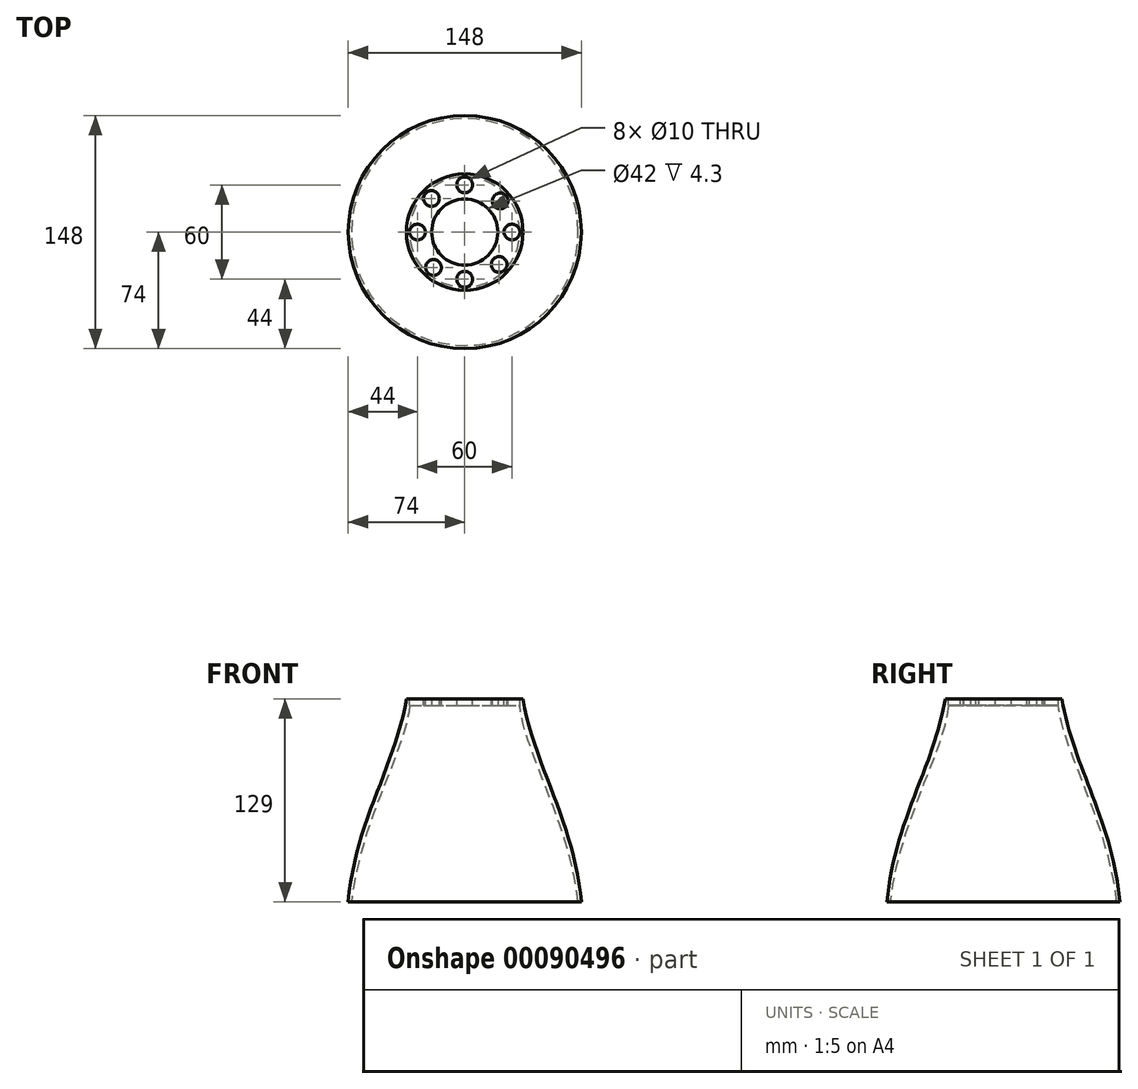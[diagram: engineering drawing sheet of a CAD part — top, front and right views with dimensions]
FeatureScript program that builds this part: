
annotation { "Feature Type Name" : "Feature", "Feature Type Description" : "" }
export const myFeature = defineFeature(function(context is Context, id is Id, definition is map)
    precondition{}
    {
        {
            var Q0;
            Q0=qCreatedBy(makeId("Front.planeOp"),FACE);
            var sketch = newSketch(context, id + "F0", { "sketchPlane" : qUnion([Q0])});
            skLineSegment(sketch, "E0", {"start": v(0, -39.7) * mm, "end": v(0, 161.4) * mm, "construction": true});
            skLineSegment(sketch, "E1", {"start": v(0, 125) * mm, "end": v(0, 129) * mm});
            skLineSegment(sketch, "E2", {"start": v(-21, 136.48) * mm, "end": v(-21, 88.58) * mm, "construction": true});
            skLineSegment(sketch, "E3", {"start": v(-37, 129) * mm, "end": v(-21, 129) * mm});
            skLineSegment(sketch, "E4", {"start": v(-21, 129) * mm, "end": v(-21, 124.7) * mm});
            skLineSegment(sketch, "E5", {"start": v(-21, 124.7) * mm, "end": v(-35, 124.7) * mm});
            skFitSpline(sketch, "E6", {"points": [v(-35, 124.7) * mm, v(-72, 0) * mm], "startDerivative": vector(-8.23, -87.48) * mm, "endDerivative": vector(-16.47, -151.8) * mm});
            skFitSpline(sketch, "E7", {"points": [v(-37, 129) * mm, v(-74, 0) * mm], "startDerivative": vector(-21.8, -129.2) * mm, "endDerivative": vector(-12.35, -149.73) * mm});
            skLineSegment(sketch, "E8", {"start": v(-74, 0) * mm, "end": v(-72, 0) * mm});
            skSolve(sketch);
        }
        {
            var Q0;
            Q0=qCreatedBy(makeId("Top.planeOp"),FACE);
            var sketch = newSketch(context, id + "F1", { "sketchPlane" : qUnion([Q0])});
            skCircle(sketch, "E9", {"center": v(0, 0) * mm, "radius": 30 * mm, "construction": true});
            skCircle(sketch, "E10", {"center": v(0, 30) * mm, "radius": 5 * mm});
            skCircle(sketch, "E11", {"center": v(-30, 0) * mm, "radius": 5 * mm});
            skCircle(sketch, "E12", {"center": v(0, -30) * mm, "radius": 5 * mm});
            skCircle(sketch, "E13", {"center": v(30, 0) * mm, "radius": 5 * mm});
            skCircle(sketch, "E14", {"center": v(-19.81, -22.53) * mm, "radius": 5 * mm});
            skCircle(sketch, "E15", {"center": v(22.55, 19.78) * mm, "radius": 5 * mm});
            skCircle(sketch, "E16", {"center": v(-21.14, 21.28) * mm, "radius": 5 * mm});
            skCircle(sketch, "E17", {"center": v(21.86, -20.55) * mm, "radius": 5 * mm});
            skSolve(sketch);
        }
        {
            var Q0;
            Q0=qSketchRegion(id+"F0",true);
            var Q1;
            Q1=sQuery(id+"F0.wireOp",EDGE,"E0");
            revolve(context, id + "F2", {"entities" : qUnion([Q0]), "axis" : qUnion([Q1]), "revolveType" : RevolveType.FULL});
        }
        {
            var Q0;
            Q0=qSketchRegion(id+"F1",true);
            extrude(context, id + "F3", {"entities" : qUnion([Q0]), "operationType" : NewBodyOperationType.REMOVE, "endBound" : BoundingType.SYMMETRIC, "oppositeDirection" : true, "depth" : 300 * mm});
        }
    });
